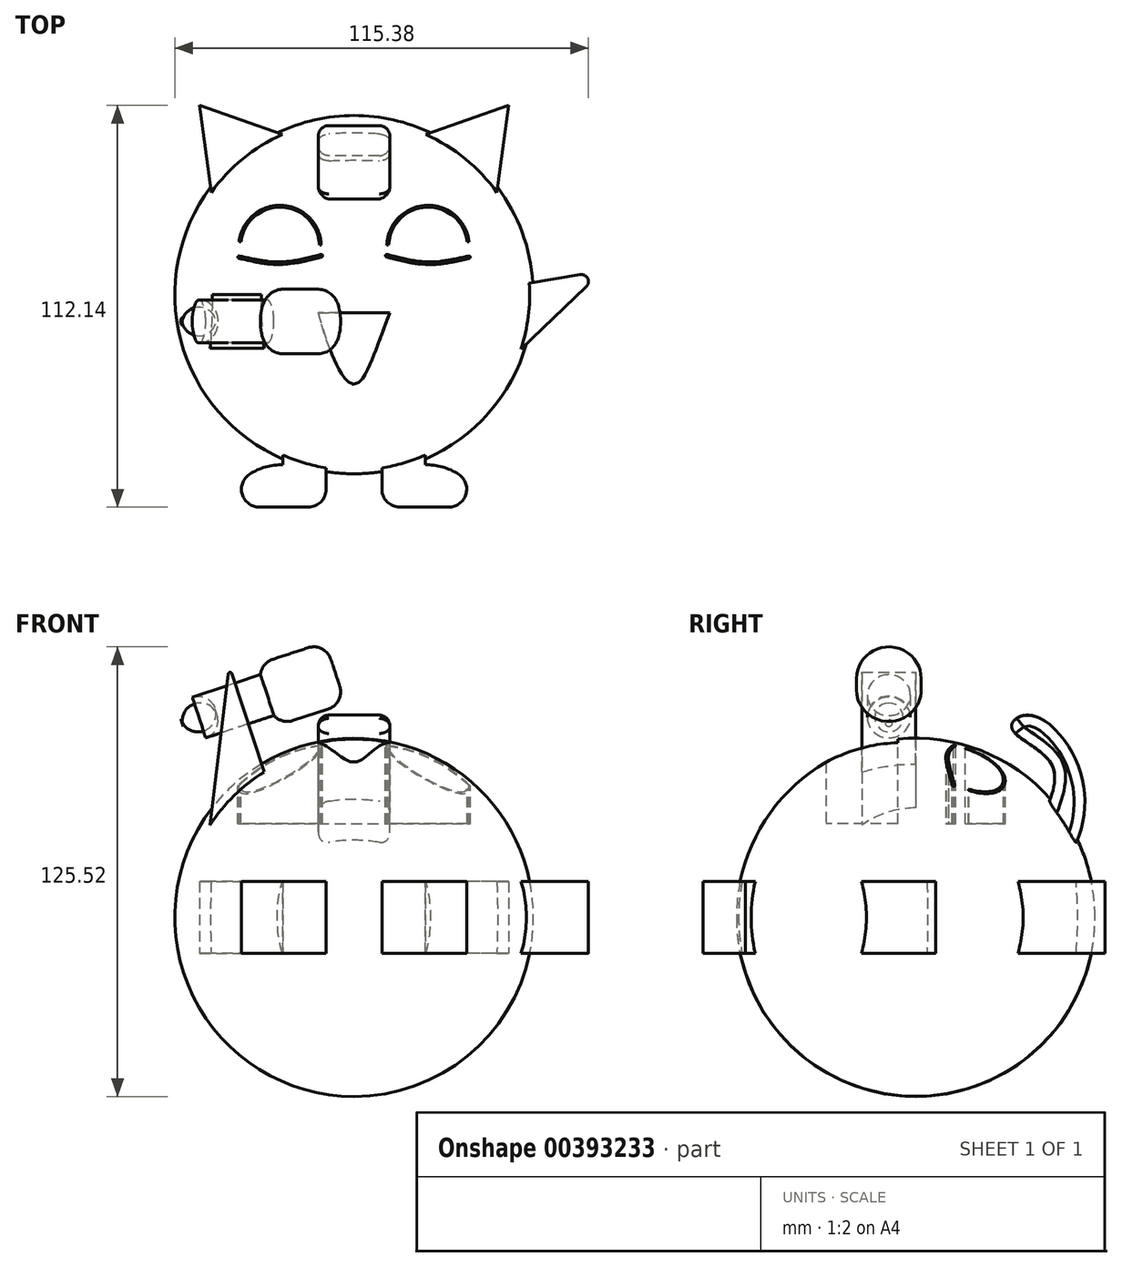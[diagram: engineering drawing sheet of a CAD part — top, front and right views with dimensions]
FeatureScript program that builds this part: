
annotation { "Feature Type Name" : "Feature", "Feature Type Description" : "" }
export const myFeature = defineFeature(function(context is Context, id is Id, definition is map)
    precondition{}
    {
        {
            var Q0;
            Q0=qCreatedBy(makeId("Top.planeOp"),FACE);
            var sketch = newSketch(context, id + "F0", { "sketchPlane" : qUnion([Q0])});
            skCircle(sketch, "E0", {"center": v(0, 0) * mm, "radius": 50 * mm});
            skLineSegment(sketch, "E1", {"start": v(0, 50) * mm, "end": v(0, -50) * mm});
            skSolve(sketch);
        }
        {
            var Q0;
            {var subQ0=sQuery(id+"F0.wireOp",EDGE,"E1");Q0=makeQuery(id+"F0.imprint","IMPRINT",FACE,{"disambiguationData":[TD([[makeQuery(id+"F0.imprint","IMPRINT",EDGE,{"derivedFrom":subQ0}),1.0]])]});}
            var Q1;
            Q1=sQuery(id+"F0.wireOp",EDGE,"E1");
            revolve(context, id + "F1", {"entities" : qUnion([Q0]), "axis" : qUnion([Q1]), "revolveType" : RevolveType.FULL});
        }
        {
            var Q0;
            Q0=qCreatedBy(makeId("Top.planeOp"),FACE);
            var sketch = newSketch(context, id + "F2", { "sketchPlane" : qUnion([Q0])});
            skLineSegment(sketch, "E2", {"start": v(0, 0) * mm, "end": v(0, 82.85) * mm, "construction": true});
            skLineSegment(sketch, "E3", {"start": v(-39.11, 23) * mm, "end": v(-43.06, 52.83) * mm});
            skLineSegment(sketch, "E4", {"start": v(-43.06, 52.83) * mm, "end": v(-13.88, 42.52) * mm});
            skLineSegment(sketch, "E5.MirrorCS", {"start": v(43.06, 52.83) * mm, "end": v(13.88, 42.52) * mm});
            skLineSegment(sketch, "E6.MirrorCS", {"start": v(39.11, 23) * mm, "end": v(43.06, 52.83) * mm});
            skLineSegment(sketch, "E7", {"start": v(-39.11, 23) * mm, "end": v(-13.88, 42.52) * mm});
            skLineSegment(sketch, "E8", {"start": v(13.88, 42.52) * mm, "end": v(39.11, 23) * mm});
            skSolve(sketch);
        }
        {
            var Q0;
            Q0 = qSketchRegion(id + "F2", true);
            extrude(context, id + "F3", {"entities" : qUnion([Q0]), "operationType" : NewBodyOperationType.ADD, "endBound" : BoundingType.SYMMETRIC, "depth" : 20 * mm});
        }
        {
            var Q0;
            Q0=qCreatedBy(makeId("Top.planeOp"),FACE);
            var sketch = newSketch(context, id + "F4", { "sketchPlane" : qUnion([Q0])});
            skLineSegment(sketch, "E9", {"start": v(41.82, 1.93) * mm, "end": v(69.52, 6.7) * mm});
            skLineSegment(sketch, "E10", {"start": v(69.52, 6.7) * mm, "end": v(43.62, -17.98) * mm});
            skLineSegment(sketch, "E11", {"start": v(43.62, -17.98) * mm, "end": v(41.82, 1.93) * mm});
            skSolve(sketch);
        }
        {
            var Q0;
            Q0 = qSketchRegion(id + "F4", true);
            extrude(context, id + "F5", {"entities" : qUnion([Q0]), "operationType" : NewBodyOperationType.ADD, "endBound" : BoundingType.SYMMETRIC, "depth" : 20 * mm});
        }
        {
            var Q0;
            Q0=qCreatedBy(makeId("Top.planeOp"),FACE);
            cPlane(context, id + "F6", {"entities" : qUnion([Q0]), "cplaneType" : CPlaneType.OFFSET, "offset" : 51.1 * mm, "width" : 150 * mm, "height" : 150 * mm});
        }
        {
            var Q0;
            Q0=qCreatedBy(id+"F6.planeOp",FACE);
            var sketch = newSketch(context, id + "F7", { "sketchPlane" : qUnion([Q0])});
            skLineSegment(sketch, "E12", {"start": v(-10, -5.03) * mm, "end": v(10, -5.03) * mm});
            skFitSpline(sketch, "E13", {"points": [v(-10, -5.03) * mm, v(0, -25.03) * mm, v(10, -5.03) * mm], "startDerivative": vector(16.3, -60.28) * mm, "endDerivative": vector(23.66, 59.74) * mm});
            skLineSegment(sketch, "E14", {"start": v(0, 63.33) * mm, "end": v(0, -68.46) * mm, "construction": true});
            skSolve(sketch);
        }
        {
            var Q0;
            Q0 = qSketchRegion(id + "F7", true);
            extrude(context, id + "F8", {"entities" : qUnion([Q0]), "operationType" : NewBodyOperationType.REMOVE, "oppositeDirection" : true, "depth" : 25 * mm});
        }
        {
            var Q0;
            Q0=qCreatedBy(makeId("Top.planeOp"),FACE);
            var sketch = newSketch(context, id + "F9", { "sketchPlane" : qUnion([Q0])});
            skLineSegment(sketch, "E15", {"start": v(-7.77, -37.43) * mm, "end": v(-7.77, -59.3) * mm});
            skLineSegment(sketch, "E16", {"start": v(-7.77, -59.3) * mm, "end": v(-35.87, -59.3) * mm});
            skArc(sketch, "E17", {"start": v(-19.84, -47.51) * mm, "mid": v(-29.9, -50.64) * mm, "end": v(-35.87, -59.3) * mm});
            skLineSegment(sketch, "E18", {"start": v(-19.84, -47.51) * mm, "end": v(-19.84, -36.07) * mm});
            skLineSegment(sketch, "E19", {"start": v(-19.84, -36.07) * mm, "end": v(-7.77, -37.43) * mm});
            skLineSegment(sketch, "E20", {"start": v(0, 0) * mm, "end": v(0, -91.2) * mm, "construction": true});
            skLineSegment(sketch, "E21.MirrorCS", {"start": v(7.77, -37.43) * mm, "end": v(7.77, -59.3) * mm});
            skLineSegment(sketch, "E22.MirrorCS", {"start": v(19.84, -36.07) * mm, "end": v(7.77, -37.43) * mm});
            skArc(sketch, "E23.MirrorCS", {"start": v(19.84, -47.51) * mm, "mid": v(29.9, -50.64) * mm, "end": v(35.87, -59.3) * mm});
            skLineSegment(sketch, "E24.MirrorCS", {"start": v(19.84, -47.51) * mm, "end": v(19.84, -36.07) * mm});
            skLineSegment(sketch, "E25.MirrorCS", {"start": v(7.77, -59.3) * mm, "end": v(35.87, -59.3) * mm});
            skSolve(sketch);
        }
        {
            var Q0;
            Q0 = qSketchRegion(id + "F9", true);
            extrude(context, id + "F10", {"entities" : qUnion([Q0]), "operationType" : NewBodyOperationType.ADD, "endBound" : BoundingType.SYMMETRIC, "depth" : 20 * mm});
        }
        {
            var Q0;
            Q0=qCreatedBy(id+"F6.planeOp",FACE);
            var sketch = newSketch(context, id + "F11", { "sketchPlane" : qUnion([Q0])});
            skArc(sketch, "E26", {"start": v(-9.14, 13.84) * mm, "mid": v(-20.19, 24.93) * mm, "end": v(-32.1, 14.77) * mm});
            skLineSegment(sketch, "E27", {"start": v(0, 68.45) * mm, "end": v(0, -74.28) * mm, "construction": true});
            skFitSpline(sketch, "E28", {"points": [v(-32.1, 10.84) * mm, v(-20.66, 9.14) * mm, v(-9.14, 11.21) * mm], "startDerivative": vector(22.95, -5.3) * mm, "endDerivative": vector(22.97, 6.04) * mm});
            skFitSpline(sketch, "E29.0", {"points": [v(-32.26, 10.16) * mm, v(-31.3, 9.94) * mm, v(-29.38, 9.5) * mm, v(-26.48, 8.92) * mm, v(-24.05, 8.58) * mm, v(-22.09, 8.44) * mm, v(-20.61, 8.42) * mm, v(-19.14, 8.5) * mm, v(-17.18, 8.7) * mm, v(-14.74, 9.1) * mm, v(-11.84, 9.78) * mm, v(-9.92, 10.29) * mm, v(-8.96, 10.54) * mm]});
            skArc(sketch, "E30", {"start": v(-8.96, 10.54) * mm, "mid": v(-8.77, 10.95) * mm, "end": v(-9.14, 11.21) * mm});
            skArc(sketch, "E31", {"start": v(-32.1, 10.84) * mm, "mid": v(-32.39, 10.55) * mm, "end": v(-32.26, 10.16) * mm});
            skArc(sketch, "E32.MirrorCS", {"start": v(8.96, 10.54) * mm, "mid": v(8.77, 10.95) * mm, "end": v(9.14, 11.21) * mm});
            skArc(sketch, "E33.MirrorCS", {"start": v(32.1, 10.84) * mm, "mid": v(32.39, 10.55) * mm, "end": v(32.26, 10.16) * mm});
            skArc(sketch, "E34.MirrorCS", {"start": v(9.14, 13.84) * mm, "mid": v(20.19, 24.93) * mm, "end": v(32.1, 14.77) * mm});
            skFitSpline(sketch, "E35.MirrorCS", {"points": [v(32.1, 10.84) * mm, v(20.66, 9.14) * mm, v(9.14, 11.21) * mm], "startDerivative": vector(-22.95, -5.3) * mm, "endDerivative": vector(-22.97, 6.04) * mm});
            skFitSpline(sketch, "E36", {"points": [v(8.96, 10.54) * mm, v(20.66, 8.4) * mm, v(32.26, 10.16) * mm], "startDerivative": vector(23.32, -6.24) * mm, "endDerivative": vector(23.27, 5.5) * mm});
            skArc(sketch, "E37.0", {"start": v(-9.64, 13.82) * mm, "mid": v(-20.21, 24.43) * mm, "end": v(-31.6, 14.7) * mm});
            skLineSegment(sketch, "E38", {"start": v(-9.64, 13.82) * mm, "end": v(-9.14, 13.84) * mm});
            skLineSegment(sketch, "E39", {"start": v(-32.1, 14.77) * mm, "end": v(-31.6, 14.7) * mm});
            skArc(sketch, "E40.0", {"start": v(9.64, 13.82) * mm, "mid": v(20.21, 24.43) * mm, "end": v(31.6, 14.7) * mm});
            skLineSegment(sketch, "E41", {"start": v(31.6, 14.7) * mm, "end": v(32.1, 14.77) * mm});
            skLineSegment(sketch, "E42", {"start": v(9.14, 13.84) * mm, "end": v(9.64, 13.82) * mm});
            skSolve(sketch);
        }
        {
            var Q0;
            Q0 = qSketchRegion(id + "F11", true);
            extrude(context, id + "F12", {"entities" : qUnion([Q0]), "operationType" : NewBodyOperationType.REMOVE, "oppositeDirection" : true, "depth" : 25 * mm});
        }
        {
            var Q0;
            Q0=qCreatedBy(makeId("Right.planeOp"),FACE);
            var sketch = newSketch(context, id + "F13", { "sketchPlane" : qUnion([Q0])});
            skFitSpline(sketch, "E43", {"points": [v(40.1, 15.68) * mm, v(46.84, 36.73) * mm, v(31.69, 56.44) * mm, v(26.78, 52.87) * mm, v(38.3, 41.8) * mm, v(34.34, 21.13) * mm, v(40.1, 15.68) * mm]});
            skSolve(sketch);
        }
        {
            var Q0;
            Q0 = qSketchRegion(id + "F13", true);
            extrude(context, id + "F14", {"entities" : qUnion([Q0]), "operationType" : NewBodyOperationType.ADD, "endBound" : BoundingType.SYMMETRIC, "depth" : 20 * mm});
        }
        {
            var Q0;
            Q0=makeQuery(id+"F10.opExtrude","SWEPT_EDGE",EDGE,{"disambiguationData":[OSD([sQuery(id+"F9.wireOp",EDGE,"E16"),sQuery(id+"F9.wireOp",EDGE,"E17")])]});
            var Q1;
            Q1=makeQuery(id+"F10.opExtrude","SWEPT_EDGE",EDGE,{"disambiguationData":[OSD([sQuery(id+"F9.wireOp",EDGE,"E23.MirrorCS"),sQuery(id+"F9.wireOp",EDGE,"E25.MirrorCS")])]});
            fillet(context, id + "F15", {"entities" : qUnion([Q0, Q1]), "radius" : 5 * mm, "tangentPropagation" : true, "allowEdgeOverflow" : false});
        }
        {
            var Q0;
            Q0=qCreatedBy(makeId("Front.planeOp"),FACE);
            var sketch = newSketch(context, id + "F16", { "sketchPlane" : qUnion([Q0])});
            skLineSegment(sketch, "E44", {"start": v(-34.8, 70.19) * mm, "end": v(-40.7, 21.24) * mm});
            skLineSegment(sketch, "E45", {"start": v(-40.7, 21.24) * mm, "end": v(-20.23, 25.74) * mm});
            skLineSegment(sketch, "E46", {"start": v(-20.23, 25.74) * mm, "end": v(-34.8, 70.19) * mm});
            skSolve(sketch);
        }
        {
            var Q0;
            Q0 = qSketchRegion(id + "F16", true);
            extrude(context, id + "F17", {"entities" : qUnion([Q0]), "operationType" : NewBodyOperationType.ADD, "depth" : 15 * mm});
        }
        {
            var Q0;
            Q0=makeQuery(id+"F17.opExtrude","SWEPT_FACE",FACE,{"disambiguationData":[OSD([sQuery(id+"F16.wireOp",EDGE,"E46")])]});
            var sketch = newSketch(context, id + "F18", { "sketchPlane" : qUnion([Q0])});
            skLineSegment(sketch, "E47", {"start": v(-7.5, 77.54) * mm, "end": v(-7.5, 51.98) * mm, "construction": true});
            skCircle(sketch, "E48", {"center": v(-7.5, 66.5) * mm, "radius": 6 * mm});
            skSolve(sketch);
        }
        {
            var Q0;
            Q0 = qSketchRegion(id + "F18", true);
            extrude(context, id + "F19", {"entities" : qUnion([Q0]), "endBound" : BoundingType.SYMMETRIC, "depth" : 35 * mm});
        }
        {
            var Q0;
            Q0=makeQuery(id+"F19.opExtrude","CAP_FACE",FACE,{"disambiguationData":[OSD([sQuery(id+"F18.wireOp",EDGE,"E48")])],"isStart":false});
            var sketch = newSketch(context, id + "F20", { "sketchPlane" : qUnion([Q0])});
            skCircle(sketch, "E49", {"center": v(-7.5, 66.5) * mm, "radius": 9 * mm});
            skSolve(sketch);
        }
        {
            var Q0;
            Q0=makeQuery(id+"F20.imprint","IMPRINT",FACE,{"disambiguationData":[TD([[makeQuery(id+"F20.imprint","IMPRINT",EDGE,{"derivedFrom":sQuery(id+"F20.wireOp",EDGE,"E49")}),1.0]])]});
            var Q1;
            Q1=makeQuery(id+"F20.imprint","IMPRINT",FACE,{"disambiguationData":[TD([[makeQuery(id+"F20.imprint","IMPRINT",EDGE,{"derivedFrom":makeQuery(id+"F19.opExtrude","CAP_EDGE",EDGE,{"disambiguationData":[OSD([sQuery(id+"F18.wireOp",EDGE,"E48")])],"isStart":false})}),1.0]])]});
            extrude(context, id + "F21", {"entities" : qUnion([Q0, Q1]), "operationType" : NewBodyOperationType.ADD, "endBound" : BoundingType.SYMMETRIC, "depth" : 20 * mm});
        }
        {
            var Q0;
            Q0=makeQuery(id+"F21.opExtrude","CAP_EDGE",EDGE,{"disambiguationData":[OSD([sQuery(id+"F20.wireOp",EDGE,"E49")])],"isStart":true});
            var Q1;
            Q1=makeQuery(id+"F21.opExtrude","CAP_EDGE",EDGE,{"disambiguationData":[OSD([sQuery(id+"F20.wireOp",EDGE,"E49")])],"isStart":false});
            fillet(context, id + "F22", {"entities" : qUnion([Q0, Q1]), "radius" : 5 * mm, "tangentPropagation" : true, "allowEdgeOverflow" : false});
        }
        {
            var Q0;
            Q0=makeQuery(id+"F19.opExtrude","CAP_EDGE",EDGE,{"disambiguationData":[OSD([sQuery(id+"F18.wireOp",EDGE,"E48")])],"isStart":true});
            fillet(context, id + "F23", {"entities" : qUnion([Q0]), "radius" : 5 * mm, "tangentPropagation" : true, "allowEdgeOverflow" : false});
        }
        {
            var Q0;
            Q0=makeQuery(id+"F17.opExtrude","SWEPT_EDGE",EDGE,{"disambiguationData":[OSD([sQuery(id+"F16.wireOp",EDGE,"E44"),sQuery(id+"F16.wireOp",EDGE,"E46")])]});
            fillet(context, id + "F24", {"entities" : qUnion([Q0]), "radius" : 0.5 * mm, "tangentPropagation" : true, "allowEdgeOverflow" : false});
        }
        {
            var Q0;
            Q0=makeQuery(id+"F5.opExtrude","SWEPT_EDGE",EDGE,{"disambiguationData":[OSD([sQuery(id+"F4.wireOp",EDGE,"E9"),sQuery(id+"F4.wireOp",EDGE,"E10")])]});
            fillet(context, id + "F25", {"entities" : qUnion([Q0]), "radius" : 2 * mm, "tangentPropagation" : true, "allowEdgeOverflow" : false});
        }
        {
            var Q0;
            Q0=makeQuery(id+"F14.opExtrude","CAP_EDGE",EDGE,{"disambiguationData":[OSD([sQuery(id+"F13.wireOp",EDGE,"E43")])],"isStart":false});
            var Q1;
            Q1=makeQuery(id+"F14.opExtrude","CAP_EDGE",EDGE,{"disambiguationData":[OSD([sQuery(id+"F13.wireOp",EDGE,"E43")])],"isStart":true});
            fillet(context, id + "F26", {"entities" : qUnion([Q0, Q1]), "radius" : 3 * mm, "tangentPropagation" : true, "allowEdgeOverflow" : false});
        }
        {
            var Q0;
            Q0=makeQuery(id+"F10.opExtrude","SWEPT_EDGE",EDGE,{"disambiguationData":[OSD([sQuery(id+"F9.wireOp",EDGE,"E15"),sQuery(id+"F9.wireOp",EDGE,"E16")])]});
            var Q1;
            Q1=makeQuery(id+"F10.opExtrude","SWEPT_EDGE",EDGE,{"disambiguationData":[OSD([sQuery(id+"F9.wireOp",EDGE,"E21.MirrorCS"),sQuery(id+"F9.wireOp",EDGE,"E25.MirrorCS")])]});
            fillet(context, id + "F27", {"entities" : qUnion([Q0, Q1]), "radius" : 5 * mm, "tangentPropagation" : true, "allowEdgeOverflow" : false});
        }
    });
